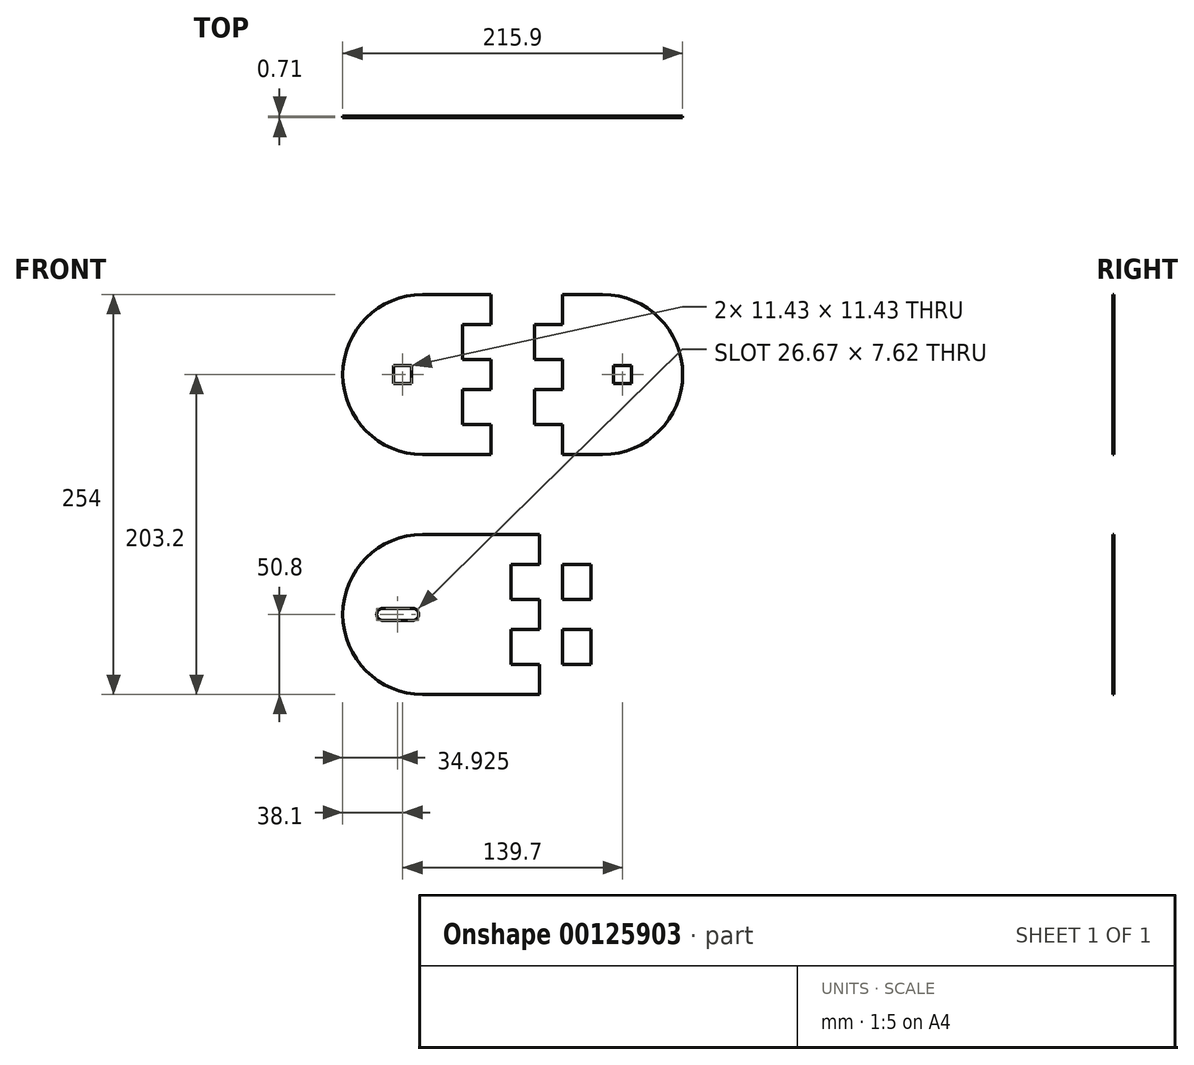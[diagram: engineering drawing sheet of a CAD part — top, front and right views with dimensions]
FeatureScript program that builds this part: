
annotation { "Feature Type Name" : "Feature", "Feature Type Description" : "" }
export const myFeature = defineFeature(function(context is Context, id is Id, definition is map)
    precondition{}
    {
        {
            assignVariable(context, id + "F0", {"name" : "ply34", "anyValue" : 0.71});
        }
        {
            var Q0;
            Q0=qCreatedBy(makeId("Front.planeOp"),FACE);
            var sketch = newSketch(context, id + "F1", { "sketchPlane" : qUnion([Q0])});
            skLineSegment(sketch, "E0.bottom", {"start": v(0, 0) * mm, "end": v(-25.4, 0) * mm});
            skLineSegment(sketch, "E0.top", {"start": v(0, 101.6) * mm, "end": v(-25.4, 101.6) * mm});
            skLineSegment(sketch, "E0.left", {"start": v(0, 0) * mm, "end": v(0, 101.6) * mm});
            skLineSegment(sketch, "E0.right", {"start": v(-76.2, 50.8) * mm, "end": v(-76.2, 50.8) * mm});
            skLineSegment(sketch, "E1.bottom", {"start": v(0, 101.6) * mm, "end": v(18.03, 101.6) * mm});
            skLineSegment(sketch, "E1.top", {"start": v(0, 82.55) * mm, "end": v(18.03, 82.55) * mm});
            skLineSegment(sketch, "E1.left", {"start": v(0, 101.6) * mm, "end": v(0, 82.55) * mm});
            skLineSegment(sketch, "E1.right", {"start": v(18.03, 101.6) * mm, "end": v(18.03, 82.55) * mm});
            skLineSegment(sketch, "E2.bottom", {"start": v(0, 60.33) * mm, "end": v(18.03, 60.33) * mm});
            skLineSegment(sketch, "E2.top", {"start": v(0, 41.27) * mm, "end": v(18.03, 41.27) * mm});
            skLineSegment(sketch, "E2.left", {"start": v(0, 60.33) * mm, "end": v(0, 41.28) * mm});
            skLineSegment(sketch, "E2.right", {"start": v(18.03, 60.33) * mm, "end": v(18.03, 41.28) * mm});
            skLineSegment(sketch, "E3.bottom", {"start": v(0, 0) * mm, "end": v(18.03, 0) * mm});
            skLineSegment(sketch, "E3.top", {"start": v(0, 19.05) * mm, "end": v(18.03, 19.05) * mm});
            skLineSegment(sketch, "E3.left", {"start": v(0, 0) * mm, "end": v(0, 19.05) * mm});
            skLineSegment(sketch, "E3.right", {"start": v(18.03, 0) * mm, "end": v(18.03, 19.05) * mm});
            skPoint(sketch, "E4", {"position": v(0, 50.8) * mm});
            skLineSegment(sketch, "E5.bottom", {"start": v(88.9, 101.6) * mm, "end": v(63.5, 101.6) * mm});
            skLineSegment(sketch, "E5.top", {"start": v(88.9, 0) * mm, "end": v(63.5, 0) * mm});
            skLineSegment(sketch, "E5.left", {"start": v(139.7, 50.8) * mm, "end": v(139.7, 50.8) * mm});
            skLineSegment(sketch, "E5.right", {"start": v(63.5, 101.6) * mm, "end": v(63.5, 0) * mm});
            skLineSegment(sketch, "E6.bottom", {"start": v(63.5, 82.55) * mm, "end": v(45.47, 82.55) * mm});
            skLineSegment(sketch, "E6.top", {"start": v(63.5, 60.33) * mm, "end": v(45.47, 60.33) * mm});
            skLineSegment(sketch, "E6.left", {"start": v(63.5, 82.55) * mm, "end": v(63.5, 60.33) * mm});
            skLineSegment(sketch, "E6.right", {"start": v(45.47, 82.55) * mm, "end": v(45.47, 60.33) * mm});
            skLineSegment(sketch, "E7.bottom", {"start": v(63.5, 19.05) * mm, "end": v(45.47, 19.05) * mm});
            skLineSegment(sketch, "E7.top", {"start": v(63.5, 41.27) * mm, "end": v(45.47, 41.27) * mm});
            skLineSegment(sketch, "E7.left", {"start": v(63.5, 19.05) * mm, "end": v(63.5, 41.28) * mm});
            skLineSegment(sketch, "E7.right", {"start": v(45.47, 19.05) * mm, "end": v(45.47, 41.28) * mm});
            skLineSegment(sketch, "E8.bottom", {"start": v(-457.2, 228.6) * mm, "end": v(-203.2, 228.6) * mm, "construction": true});
            skLineSegment(sketch, "E8.top", {"start": v(-457.2, -228.6) * mm, "end": v(-203.2, -228.6) * mm, "construction": true});
            skLineSegment(sketch, "E8.left", {"start": v(-457.2, 228.6) * mm, "end": v(-457.2, -228.6) * mm, "construction": true});
            skLineSegment(sketch, "E8.right", {"start": v(-203.2, 228.6) * mm, "end": v(-203.2, -228.6) * mm, "construction": true});
            skPoint(sketch, "E8.middle", {"position": v(-330.2, 0) * mm});
            skLineSegment(sketch, "E9.bottom", {"start": v(-250.83, 25.4) * mm, "end": v(-234.95, 25.4) * mm, "construction": true});
            skLineSegment(sketch, "E9.top", {"start": v(-250.83, -25.4) * mm, "end": v(-234.95, -25.4) * mm, "construction": true});
            skLineSegment(sketch, "E9.left", {"start": v(-250.82, 25.4) * mm, "end": v(-250.82, -25.4) * mm, "construction": true});
            skLineSegment(sketch, "E9.right", {"start": v(-234.95, 25.4) * mm, "end": v(-234.95, -25.4) * mm, "construction": true});
            skPoint(sketch, "E9.middle", {"position": v(-242.89, 0) * mm});
            skPoint(sketch, "E10.middle.positionSnap0", {"position": v(-38.1, 0) * mm});
            skPoint(sketch, "E10.centerSnap0", {"position": v(-38.1, 0) * mm});
            skLineSegment(sketch, "E11", {"start": v(0, -12.7) * mm, "end": v(63.5, -12.7) * mm, "construction": true});
            skLineSegment(sketch, "E12", {"start": v(31.75, -12.7) * mm, "end": v(31.75, 0) * mm, "construction": true});
            skLineSegment(sketch, "E13.bottom", {"start": v(-25.4, -50.8) * mm, "end": v(30.73, -50.8) * mm});
            skLineSegment(sketch, "E13.top", {"start": v(-25.4, -152.4) * mm, "end": v(30.73, -152.4) * mm});
            skLineSegment(sketch, "E13.left", {"start": v(-76.2, -101.6) * mm, "end": v(-76.2, -101.6) * mm});
            skLineSegment(sketch, "E13.right", {"start": v(30.73, -50.8) * mm, "end": v(30.73, -152.4) * mm});
            skLineSegment(sketch, "E14.bottom", {"start": v(30.73, -50.8) * mm, "end": v(48.77, -50.8) * mm});
            skLineSegment(sketch, "E14.top", {"start": v(30.73, -69.85) * mm, "end": v(48.77, -69.85) * mm});
            skLineSegment(sketch, "E14.left", {"start": v(30.73, -50.8) * mm, "end": v(30.73, -69.85) * mm});
            skLineSegment(sketch, "E14.right", {"start": v(48.77, -50.8) * mm, "end": v(48.77, -69.85) * mm});
            skLineSegment(sketch, "E15.bottom", {"start": v(30.73, -152.4) * mm, "end": v(48.77, -152.4) * mm});
            skLineSegment(sketch, "E15.top", {"start": v(30.73, -133.35) * mm, "end": v(48.77, -133.35) * mm});
            skLineSegment(sketch, "E15.left", {"start": v(30.73, -152.4) * mm, "end": v(30.73, -133.35) * mm});
            skLineSegment(sketch, "E15.right", {"start": v(48.77, -152.4) * mm, "end": v(48.77, -133.35) * mm});
            skLineSegment(sketch, "E16.bottom", {"start": v(30.73, -92.08) * mm, "end": v(48.77, -92.08) * mm});
            skLineSegment(sketch, "E16.top", {"start": v(30.73, -111.13) * mm, "end": v(48.77, -111.13) * mm});
            skLineSegment(sketch, "E16.left", {"start": v(30.73, -92.08) * mm, "end": v(30.73, -111.12) * mm});
            skLineSegment(sketch, "E16.right", {"start": v(48.77, -92.07) * mm, "end": v(48.77, -111.13) * mm});
            skPoint(sketch, "E16.middle", {"position": v(39.75, -101.6) * mm});
            skPoint(sketch, "E16.middle.positionSnap0", {"position": v(39.75, -69.85) * mm});
            skPoint(sketch, "E16.middle.positionSnap1", {"position": v(30.73, -101.6) * mm});
            skPoint(sketch, "E16.centerSnap0", {"position": v(39.75, -69.85) * mm});
            skPoint(sketch, "E16.centerSnap1", {"position": v(30.73, -101.6) * mm});
            skLineSegment(sketch, "E17.left", {"start": v(81.53, -50.8) * mm, "end": v(81.53, -152.4) * mm});
            skLineSegment(sketch, "E18.bottom", {"start": v(81.53, -69.85) * mm, "end": v(63.5, -69.85) * mm});
            skLineSegment(sketch, "E18.top", {"start": v(81.53, -92.08) * mm, "end": v(63.5, -92.08) * mm});
            skLineSegment(sketch, "E18.left", {"start": v(81.53, -69.85) * mm, "end": v(81.53, -92.08) * mm});
            skLineSegment(sketch, "E18.right", {"start": v(63.5, -69.85) * mm, "end": v(63.5, -92.07) * mm});
            skLineSegment(sketch, "E19.bottom", {"start": v(81.53, -111.13) * mm, "end": v(63.5, -111.13) * mm});
            skLineSegment(sketch, "E19.top", {"start": v(81.53, -133.35) * mm, "end": v(63.5, -133.35) * mm});
            skLineSegment(sketch, "E19.left", {"start": v(81.53, -111.13) * mm, "end": v(81.53, -133.35) * mm});
            skLineSegment(sketch, "E19.right", {"start": v(63.5, -111.13) * mm, "end": v(63.5, -133.35) * mm});
            skPoint(sketch, "E20.middle.positionSnap0", {"position": v(-76.2, -101.6) * mm});
            skPoint(sketch, "E20.centerSnap0", {"position": v(-76.2, -101.6) * mm});
            skLineSegment(sketch, "E21", {"start": v(48.77, -80.96) * mm, "end": v(63.5, -80.96) * mm, "construction": true});
            skLineSegment(sketch, "E22", {"start": v(56.13, -80.96) * mm, "end": v(56.13, -69.85) * mm, "construction": true});
            skPoint(sketch, "E23", {"position": v(-38.1, 50.8) * mm});
            skPoint(sketch, "E23.positionSnap0", {"position": v(-38.1, 101.6) * mm});
            skPoint(sketch, "E24", {"position": v(-38.1, -101.6) * mm});
            skCircle(sketch, "E25", {"center": v(-38.1, 50.8) * mm, "radius": 3.81 * mm});
            skCircle(sketch, "E26.MirrorC", {"center": v(101.6, 50.8) * mm, "radius": 3.81 * mm});
            skPoint(sketch, "E27.visualSharp", {"position": v(-76.2, 101.6) * mm});
            skArc(sketch, "E27.filletArc", {"start": v(-25.4, 101.6) * mm, "mid": v(-61.32, 86.72) * mm, "end": v(-76.2, 50.8) * mm});
            skPoint(sketch, "E28.visualSharp", {"position": v(-76.2, 0) * mm});
            skArc(sketch, "E28.filletArc", {"start": v(-76.2, 50.8) * mm, "mid": v(-61.32, 14.88) * mm, "end": v(-25.4, 0) * mm});
            skPoint(sketch, "E29.visualSharp", {"position": v(139.7, 101.6) * mm});
            skArc(sketch, "E29.filletArc", {"start": v(139.7, 50.8) * mm, "mid": v(124.82, 86.72) * mm, "end": v(88.9, 101.6) * mm});
            skPoint(sketch, "E30.visualSharp", {"position": v(139.7, 0) * mm});
            skArc(sketch, "E30.filletArc", {"start": v(88.9, 0) * mm, "mid": v(124.82, 14.88) * mm, "end": v(139.7, 50.8) * mm});
            skPoint(sketch, "E31.visualSharp", {"position": v(-76.2, -50.8) * mm});
            skArc(sketch, "E31.filletArc", {"start": v(-25.4, -50.8) * mm, "mid": v(-61.32, -65.68) * mm, "end": v(-76.2, -101.6) * mm});
            skPoint(sketch, "E32.visualSharp", {"position": v(-76.2, -152.4) * mm});
            skArc(sketch, "E32.filletArc", {"start": v(-76.2, -101.6) * mm, "mid": v(-61.32, -137.52) * mm, "end": v(-25.4, -152.4) * mm});
            skLineSegment(sketch, "E33.MirrorCS", {"start": v(137.67, -50.8) * mm, "end": v(81.53, -50.8) * mm});
            skArc(sketch, "E34.MirrorCS", {"start": v(137.67, -50.8) * mm, "mid": v(173.59, -65.68) * mm, "end": v(188.47, -101.6) * mm});
            skArc(sketch, "E35.MirrorCS", {"start": v(188.47, -101.6) * mm, "mid": v(173.59, -137.52) * mm, "end": v(137.67, -152.4) * mm});
            skLineSegment(sketch, "E36.MirrorCS", {"start": v(137.67, -152.4) * mm, "end": v(81.53, -152.4) * mm});
            skLineSegment(sketch, "E37", {"start": v(-50.8, -101.6) * mm, "end": v(-31.75, -101.6) * mm});
            skArc(sketch, "E38.0.startCap", {"start": v(-50.8, -105.4) * mm, "mid": v(-54.6, -101.6) * mm, "end": v(-50.8, -97.8) * mm});
            skArc(sketch, "E38.0.endCap", {"start": v(-31.75, -97.8) * mm, "mid": v(-27.94, -101.6) * mm, "end": v(-31.75, -105.4) * mm});
            skLineSegment(sketch, "E38.0.left", {"start": v(-50.8, -97.8) * mm, "end": v(-31.75, -97.8) * mm});
            skLineSegment(sketch, "E38.0.right", {"start": v(-50.8, -105.4) * mm, "end": v(-31.75, -105.4) * mm});
            skArc(sketch, "E39.MirrorCS", {"start": v(144.02, -97.8) * mm, "mid": v(140.2, -101.6) * mm, "end": v(144.02, -105.4) * mm});
            skLineSegment(sketch, "E40.MirrorCS", {"start": v(163.07, -105.4) * mm, "end": v(144.02, -105.4) * mm});
            skLineSegment(sketch, "E41.MirrorCS", {"start": v(163.07, -97.8) * mm, "end": v(144.02, -97.8) * mm});
            skArc(sketch, "E42.MirrorCS", {"start": v(163.07, -105.4) * mm, "mid": v(166.88, -101.6) * mm, "end": v(163.07, -97.8) * mm});
            skLineSegment(sketch, "E43.bottom", {"start": v(-43.82, 56.52) * mm, "end": v(-32.39, 56.52) * mm});
            skLineSegment(sketch, "E43.top", {"start": v(-43.82, 45.09) * mm, "end": v(-32.39, 45.09) * mm});
            skLineSegment(sketch, "E43.left", {"start": v(-43.82, 56.52) * mm, "end": v(-43.82, 45.09) * mm});
            skLineSegment(sketch, "E43.right", {"start": v(-32.39, 56.52) * mm, "end": v(-32.39, 45.09) * mm});
            skLineSegment(sketch, "E44.MirrorCS", {"start": v(107.32, 56.52) * mm, "end": v(95.89, 56.52) * mm});
            skLineSegment(sketch, "E45.MirrorCS", {"start": v(107.32, 56.52) * mm, "end": v(107.32, 45.09) * mm});
            skLineSegment(sketch, "E46.MirrorCS", {"start": v(95.89, 56.52) * mm, "end": v(95.89, 45.09) * mm});
            skLineSegment(sketch, "E47.MirrorCS", {"start": v(107.32, 45.09) * mm, "end": v(95.89, 45.09) * mm});
            skSolve(sketch);
        }
        {
            var Q0;
            Q0=makeQuery(id+"F1.imprint","IMPRINT",FACE,{"disambiguationData":[TD([[makeQuery(id+"F1.imprint","IMPRINT",EDGE,{"derivedFrom":sQuery(id+"F1.wireOp",EDGE,"E0.bottom")}),-1.0]])]});
            var Q1;
            Q1=makeQuery(id+"F1.imprint","IMPRINT",FACE,{"disambiguationData":[TD([[makeQuery(id+"F1.imprint","IMPRINT",EDGE,{"derivedFrom":sQuery(id+"F1.wireOp",EDGE,"E1.bottom")}),-1.0]])]});
            var Q2;
            Q2=makeQuery(id+"F1.imprint","IMPRINT",FACE,{"disambiguationData":[TD([[makeQuery(id+"F1.imprint","IMPRINT",EDGE,{"derivedFrom":sQuery(id+"F1.wireOp",EDGE,"E2.bottom")}),-1.0]])]});
            var Q3;
            Q3=makeQuery(id+"F1.imprint","IMPRINT",FACE,{"disambiguationData":[TD([[makeQuery(id+"F1.imprint","IMPRINT",EDGE,{"derivedFrom":sQuery(id+"F1.wireOp",EDGE,"E3.bottom")}),1.0]])]});
            var Q4;
            Q4=makeQuery(id+"F1.imprint","IMPRINT",FACE,{"disambiguationData":[TD([[makeQuery(id+"F1.imprint","IMPRINT",EDGE,{"derivedFrom":sQuery(id+"F1.wireOp",EDGE,"E7.bottom")}),-1.0]])]});
            var Q5;
            Q5=makeQuery(id+"F1.imprint","IMPRINT",FACE,{"disambiguationData":[TD([[makeQuery(id+"F1.imprint","IMPRINT",EDGE,{"derivedFrom":sQuery(id+"F1.wireOp",EDGE,"E6.bottom")}),1.0]])]});
            var Q6;
            {var subQ1=sQuery(id+"F1.wireOp",EDGE,"E5.bottom");Q6=makeQuery(id+"F1.imprint","IMPRINT",FACE,{"disambiguationData":[TD([[makeQuery(id+"F1.imprint","IMPRINT",EDGE,{"derivedFrom":subQ1}),1.0]])]});}
            var Q7;
            Q7=makeQuery(id+"F1.imprint","IMPRINT",FACE,{"disambiguationData":[TD([[makeQuery(id+"F1.imprint","IMPRINT",EDGE,{"derivedFrom":sQuery(id+"F1.wireOp",EDGE,"E16.bottom")}),-1.0]])]});
            var Q8;
            Q8=makeQuery(id+"F1.imprint","IMPRINT",FACE,{"disambiguationData":[TD([[makeQuery(id+"F1.imprint","IMPRINT",EDGE,{"derivedFrom":sQuery(id+"F1.wireOp",EDGE,"E13.bottom")}),-1.0]])]});
            var Q9;
            Q9=makeQuery(id+"F1.imprint","IMPRINT",FACE,{"disambiguationData":[TD([[makeQuery(id+"F1.imprint","IMPRINT",EDGE,{"derivedFrom":sQuery(id+"F1.wireOp",EDGE,"E15.bottom")}),1.0]])]});
            var Q10;
            Q10=makeQuery(id+"F1.imprint","IMPRINT",FACE,{"disambiguationData":[TD([[makeQuery(id+"F1.imprint","IMPRINT",EDGE,{"derivedFrom":sQuery(id+"F1.wireOp",EDGE,"E18.bottom")}),1.0]])]});
            var Q11;
            {var subQ1=sQuery(id+"F1.wireOp",EDGE,"E17.bottom");Q11=makeQuery(id+"F1.imprint","IMPRINT",FACE,{"disambiguationData":[TD([[makeQuery(id+"F1.imprint","IMPRINT",EDGE,{"derivedFrom":subQ1}),-1.0]])]});}
            var Q12;
            Q12=makeQuery(id+"F1.imprint","IMPRINT",FACE,{"disambiguationData":[TD([[makeQuery(id+"F1.imprint","IMPRINT",EDGE,{"derivedFrom":sQuery(id+"F1.wireOp",EDGE,"E19.bottom")}),1.0]])]});
            var Q13;
            Q13=makeQuery(id+"F1.imprint","IMPRINT",FACE,{"disambiguationData":[TD([[makeQuery(id+"F1.imprint","IMPRINT",EDGE,{"derivedFrom":sQuery(id+"F1.wireOp",EDGE,"E14.bottom")}),-1.0]])]});
            var Q14;
            {var subQ4=sQuery(id+"F1.wireOp",EDGE,"E18.left");Q14=makeQuery(id+"F1.imprint","IMPRINT",FACE,{"disambiguationData":[TD([[makeQuery(id+"F1.imprint","IMPRINT",EDGE,{"derivedFrom":subQ4}),1.0]])]});}
            extrude(context, id + "F2", {"entities" : qUnion([Q0, Q1, Q2, Q3, Q4, Q5, Q6, Q7, Q8, Q9, Q10, Q11, Q12, Q13, Q14]), "depth" : (getVariable(context, 'ply34')) * mm});
        }
    });
